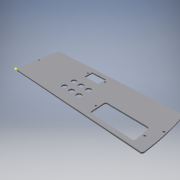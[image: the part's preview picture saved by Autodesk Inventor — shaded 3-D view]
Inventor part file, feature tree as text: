
AUTODESK INVENTOR PART (.ipt)
format: ipt  version: 2018 (Build 220112000, 112)  size: 205,312 bytes
history: native  units: mm
features: sketch x5, extrude x3, hole x1
ambient origin geometry x8: Origin, YZ Plane, XZ Plane, XY Plane, X Axis, Y Axis, Z Axis, Center Point
bodies: Volumenkörper1 (feature_tree)
feature tree (9):
  extrude  "Extrusion1"  Depth=85.0mm
  hole  "Bohrung1"  [1 undecoded]
  extrude  "Extrusion2"  Depth=2.0mm
  sketch  "Sketch7"  dims[d7=452.5625mm d8=452.5625mm]
  extrude  "Extrusion5"  Depth=452.5625mm
  sketch  "Skizze1"  dims[d0=85.0mm d1=242.0mm]
  sketch  "Skizze2"  dims[d2=2.0mm d3=2.0mm]
  sketch  "Skizze3"  dims[d4=2.0mm d5=905.125mm d6=905.125mm]
  sketch  "Sketch8"  dims[d9=2.5mm d10=0.0mm d11=42.5mm d12=42.5mm d13=235.8mm d14=117.9mm d15=117.9mm d16=3.3mm d17=6.0mm d18=4.0mm d19=2.0mm d20=90.0deg d21=8.0mm d22=20.594885mm d23=9.599311mm d24=9.599311mm d25=2.5mm d26=2.5mm d27=5.0mm d28=0.0mm d75=3.2mm d76=75.5mm d77=3.2mm d78=68.0mm d79=29.2mm d80=3.1mm d81=22.0mm d82=11.15mm d85=3.0mm d86=0.0mm d87=45.0mm d89=28.0mm d90=16.5mm d91=3.2mm d92=5.0mm d93=3.2mm d94=5.0mm d95=10.5mm d96=10.5mm d97=60.0mm d98=95.0mm d99=9.4mm d101=9.4mm d103=9.4mm d113=35.0mm d114=15.0mm d115=15.0mm d116=9.4mm d118=9.4mm d120=9.4mm d122=15.0mm d123=15.0mm d125=22.0mm d126=40.0mm d128=8.85mm d129=4.15mm]
note: 1 required parameter value undecoded (feature->parameter linkage not recoverable at this tier; creation-order binding heuristic only, values carry confidence <= 0.55)
